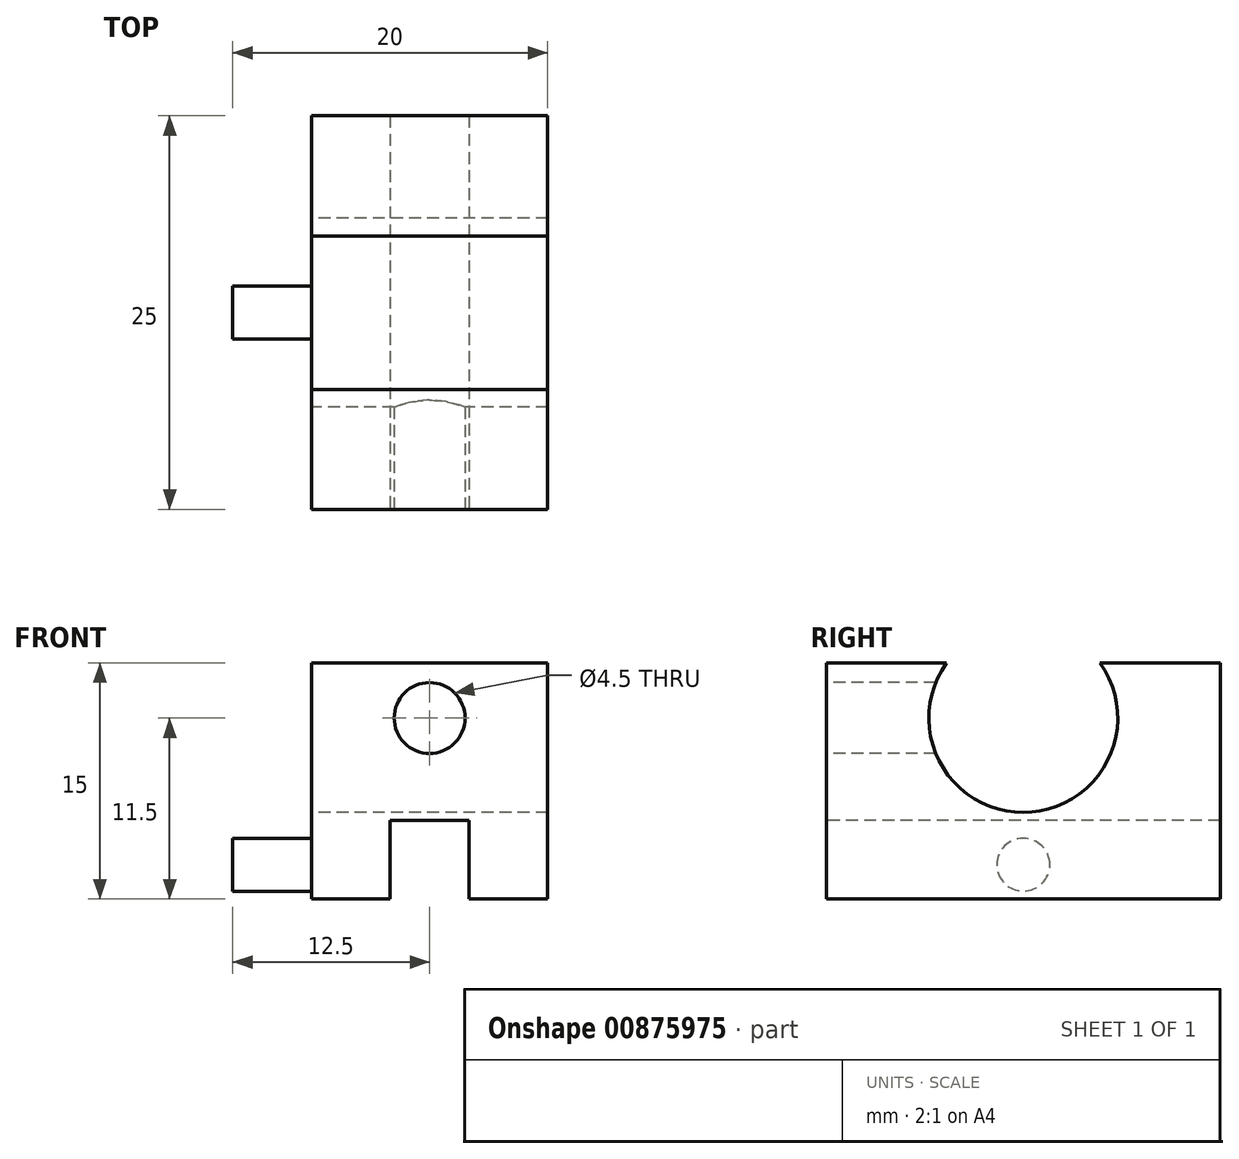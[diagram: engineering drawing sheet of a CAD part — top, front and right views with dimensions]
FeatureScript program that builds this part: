
annotation { "Feature Type Name" : "Feature", "Feature Type Description" : "" }
export const myFeature = defineFeature(function(context is Context, id is Id, definition is map)
    precondition{}
    {
        {
            var Q0;
            Q0=qCreatedBy(makeId("Front.planeOp"),FACE);
            var sketch = newSketch(context, id + "F0", { "sketchPlane" : qUnion([Q0])});
            skLineSegment(sketch, "E0.bottom", {"start": v(7.5, -7.5) * mm, "end": v(-7.5, -7.5) * mm});
            skLineSegment(sketch, "E0.top", {"start": v(7.5, 7.5) * mm, "end": v(-7.5, 7.5) * mm});
            skLineSegment(sketch, "E0.left", {"start": v(7.5, -7.5) * mm, "end": v(7.5, 7.5) * mm});
            skLineSegment(sketch, "E0.right", {"start": v(-7.5, -7.5) * mm, "end": v(-7.5, 7.5) * mm});
            skPoint(sketch, "E0.middle", {"position": v(0, 0) * mm});
            skSolve(sketch);
        }
        {
            var Q0;
            Q0 = qSketchRegion(id + "F0", true);
            extrude(context, id + "F1", {"entities" : qUnion([Q0]), "depth" : 25 * mm, "offsetDistance" : 25 * mm});
        }
        {
            var Q0;
            Q0=makeQuery(id+"F1.opExtrude","CAP_FACE",FACE,{"disambiguationData":[OSD([sQuery(id+"F0.wireOp",EDGE,"E0.bottom"),sQuery(id+"F0.wireOp",EDGE,"E0.top"),sQuery(id+"F0.wireOp",EDGE,"E0.left"),sQuery(id+"F0.wireOp",EDGE,"E0.right")])],"isStart":false});
            var sketch = newSketch(context, id + "F2", { "sketchPlane" : qUnion([Q0])});
            skLineSegment(sketch, "E1.bottom", {"start": v(2.5, -7.5) * mm, "end": v(-2.5, -7.5) * mm});
            skLineSegment(sketch, "E1.top", {"start": v(2.5, -2.5) * mm, "end": v(-2.5, -2.5) * mm});
            skLineSegment(sketch, "E1.left", {"start": v(2.5, -7.5) * mm, "end": v(2.5, -2.5) * mm});
            skLineSegment(sketch, "E1.right", {"start": v(-2.5, -7.5) * mm, "end": v(-2.5, -2.5) * mm});
            skPoint(sketch, "E1.middle", {"position": v(0, -5) * mm});
            skPoint(sketch, "E1.middle.positionSnap0", {"position": v(0, -7.5) * mm});
            skPoint(sketch, "E1.centerSnap0", {"position": v(0, -7.5) * mm});
            skSolve(sketch);
        }
        {
            var Q0;
            Q0 = qSketchRegion(id + "F2", true);
            extrude(context, id + "F3", {"entities" : qUnion([Q0]), "operationType" : NewBodyOperationType.REMOVE, "oppositeDirection" : true, "depth" : 25 * mm, "offsetDistance" : 25 * mm});
        }
        {
            var Q0;
            Q0=makeQuery(id+"F1.opExtrude","SWEPT_FACE",FACE,{"disambiguationData":[OSD([sQuery(id+"F0.wireOp",EDGE,"E0.right")])]});
            var sketch = newSketch(context, id + "F4", { "sketchPlane" : qUnion([Q0])});
            skCircle(sketch, "E2", {"center": v(12.5, 4) * mm, "radius": 6 * mm});
            skPoint(sketch, "E2.centerSnap0", {"position": v(12.5, 7.5) * mm});
            skSolve(sketch);
        }
        {
            var Q0;
            Q0=sQuery(id+"F4.wireOp",VERTEX,"E2.center");
            var Q1;
            Q1=makeQuery(id+"F1.opExtrude","SWEPT_BODY",BODY,{"disambiguationData":[OSD([sQuery(id+"F0.wireOp",EDGE,"E0.bottom"),sQuery(id+"F0.wireOp",EDGE,"E0.top"),sQuery(id+"F0.wireOp",EDGE,"E0.left"),sQuery(id+"F0.wireOp",EDGE,"E0.right")])]});
            hole(context, id + "F5", {"style" : HoleStyle.SIMPLE, "endStyle" : HoleEndStyle.THROUGH, "holeDiameter" : 12 * mm, "majorDiameter" : 5 * mm, "isTappedThrough" : true, "tappedDepth" : 12 * mm, "tapClearance" : 3, "locations" : qUnion([Q0]), "scope" : qUnion([Q1])});
        }
        {
            var Q0;
            Q0=makeQuery(id+"F1.opExtrude","SWEPT_FACE",FACE,{"disambiguationData":[OSD([sQuery(id+"F0.wireOp",EDGE,"E0.right")])]});
            var sketch = newSketch(context, id + "F6", { "sketchPlane" : qUnion([Q0])});
            skCircle(sketch, "E3", {"center": v(12.5, -5.32) * mm, "radius": 1.68 * mm});
            skPoint(sketch, "E3.centerSnap0", {"position": v(12.5, -7.5) * mm});
            skSolve(sketch);
        }
        {
            var Q0;
            Q0 = qSketchRegion(id + "F6", true);
            extrude(context, id + "F7", {"entities" : qUnion([Q0]), "operationType" : NewBodyOperationType.ADD, "depth" : 5 * mm, "offsetDistance" : 25 * mm});
        }
        {
            var Q0;
            Q0=makeQuery(id+"F1.opExtrude","CAP_FACE",FACE,{"disambiguationData":[OSD([sQuery(id+"F0.wireOp",EDGE,"E0.bottom"),sQuery(id+"F0.wireOp",EDGE,"E0.top"),sQuery(id+"F0.wireOp",EDGE,"E0.left"),sQuery(id+"F0.wireOp",EDGE,"E0.right")])],"isStart":false});
            var sketch = newSketch(context, id + "F8", { "sketchPlane" : qUnion([Q0])});
            skCircle(sketch, "E4", {"center": v(0, 4) * mm, "radius": 2.25 * mm});
            skSolve(sketch);
        }
        {
            var Q0;
            Q0=makeQuery(id+"F8.imprint","IMPRINT",FACE,{"disambiguationData":[TD([[makeQuery(id+"F8.imprint","IMPRINT",EDGE,{"derivedFrom":sQuery(id+"F8.wireOp",EDGE,"E4")}),1.0]])]});
            extrude(context, id + "F9", {"entities" : qUnion([Q0]), "operationType" : NewBodyOperationType.REMOVE, "endBound" : BoundingType.UP_TO_NEXT, "oppositeDirection" : true, "depth" : 25 * mm, "offsetDistance" : 25 * mm});
        }
    });
